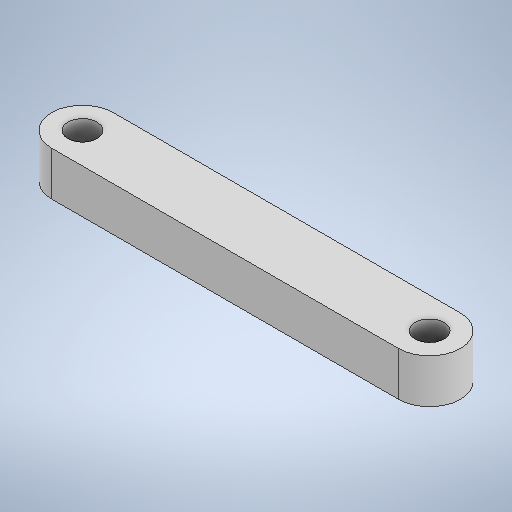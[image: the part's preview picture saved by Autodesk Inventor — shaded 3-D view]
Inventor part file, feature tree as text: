
AUTODESK INVENTOR PART (.ipt)
format: ipt  version: 2025.1 (Build 291241020, 241B)  size: 266,240 bytes
history: native  units: mm
features: move_body x2, sketch x2, other x1, extrude x1, fillet x1, split x1, boolean_combine x1, imported_body x1
ambient origin geometry x8: Origin, YZ Plane, XZ Plane, XY Plane, X Axis, Y Axis, Z Axis, Center Point
bodies: Solid1 (feature_tree), Solid2 (feature_tree), Solid3 (feature_tree), Solid4 (feature_tree)
feature tree (10):
  other  "Repaired Geometry1"
  extrude  "Extrusion1"  Depth=7.0mm
  fillet  "Fillet1"  Radius=3.3mm
  move_body  "Move Body1"
  split  "Split1"
  move_body  "Move Body2"
  boolean_combine  "Combine1"
  sketch  "Sketch1"  dims[d0=7.0mm d1=39.4mm d2=3.3mm]
  imported_body  "Base1"
  sketch  "Sketch2"  dims[d3=3.3mm d4=3.5mm d5=3.5mm d6=5.0mm d7=0.0mm d8=3.5mm d9=0.0mm d10=0.0mm d11=10.0mm d12=-0.1mm d13=0.0mm d14=0.0mm]
